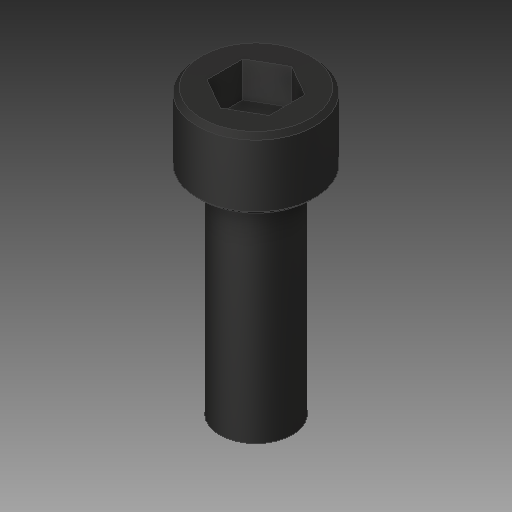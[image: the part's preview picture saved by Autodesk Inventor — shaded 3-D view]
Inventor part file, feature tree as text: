
AUTODESK INVENTOR PART (.ipt)
format: ipt  version: 2017 (Build 210142000, 142)  size: 103,424 bytes
history: native  units: in
note: dims shown in document units (in); Inventor stores cm internally (conversion verified against a paired STEP export)
features: chamfer x1
ambient origin geometry x8: Origin, YZ Plane, XZ Plane, XY Plane, X Axis, Y Axis, Z Axis, Center Point
bodies: Solid1 (feature_tree)
feature tree (1):
  chamfer  "Chamfer2"  [1 undecoded]
note: 1 required parameter value undecoded (feature->parameter linkage not recoverable at this tier; creation-order binding heuristic only, values carry confidence <= 0.55)
